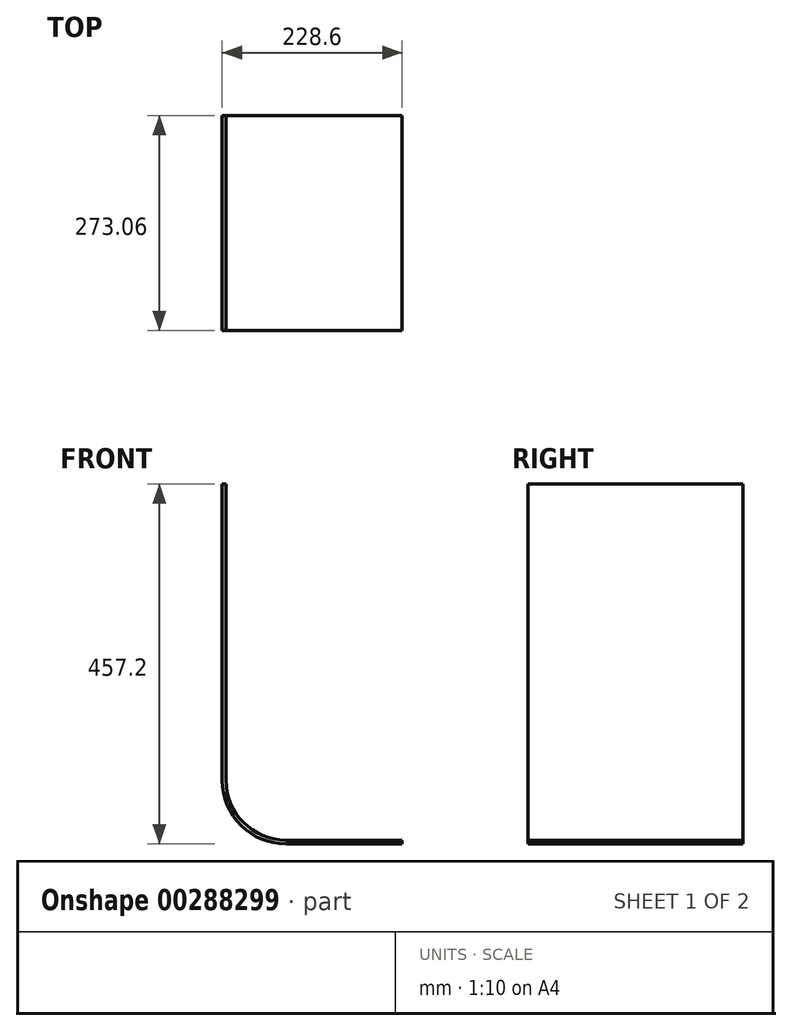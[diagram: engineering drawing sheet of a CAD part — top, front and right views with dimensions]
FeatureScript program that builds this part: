
annotation { "Feature Type Name" : "Feature", "Feature Type Description" : "" }
export const myFeature = defineFeature(function(context is Context, id is Id, definition is map)
    precondition{}
    {
        {
            var Q0;
            Q0=qCreatedBy(makeId("Front.planeOp"),FACE);
            var sketch = newSketch(context, id + "F0", { "sketchPlane" : qUnion([Q0])});
            skLineSegment(sketch, "E0", {"start": v(0, 161.93) * mm, "end": v(0, 914.4) * mm});
            skLineSegment(sketch, "E1", {"start": v(161.93, 0) * mm, "end": v(457.2, 0) * mm});
            skArc(sketch, "E2", {"start": v(0, 161.92) * mm, "mid": v(47.43, 47.43) * mm, "end": v(161.93, 0) * mm});
            skLineSegment(sketch, "E3.0", {"start": v(9.53, 161.93) * mm, "end": v(9.53, 914.4) * mm});
            skArc(sketch, "E3.1", {"start": v(9.53, 161.93) * mm, "mid": v(54.16, 54.16) * mm, "end": v(161.92, 9.53) * mm});
            skLineSegment(sketch, "E3.2", {"start": v(161.92, 9.53) * mm, "end": v(457.2, 9.53) * mm});
            skLineSegment(sketch, "E4", {"start": v(9.53, 914.4) * mm, "end": v(0, 914.4) * mm});
            skLineSegment(sketch, "E5", {"start": v(457.2, 9.53) * mm, "end": v(457.2, 0) * mm});
            skSolve(sketch);
        }
        {
            var Q0;
            Q0=qSketchRegion(id+"F0",true);
            extrude(context, id + "F1", {"entities" : qUnion([Q0]), "endBound" : BoundingType.SYMMETRIC, "depth" : 546.1 * mm});
        }
        {
            var Q0;
            Q0=makeQuery(id+"F1.opExtrude","SWEPT_BODY",BODY,{"disambiguationData":[OSD([sQuery(id+"F0.wireOp",EDGE,"E0"),sQuery(id+"F0.wireOp",EDGE,"E1"),sQuery(id+"F0.wireOp",EDGE,"E2"),sQuery(id+"F0.wireOp",EDGE,"E3.0"),sQuery(id+"F0.wireOp",EDGE,"E3.1"),sQuery(id+"F0.wireOp",EDGE,"E3.2"),sQuery(id+"F0.wireOp",EDGE,"E4"),sQuery(id+"F0.wireOp",EDGE,"E5")])]});
            var Q1;
            Q1=qCreatedBy(makeId("Origin.pointOp"),VERTEX);
            transform(context, id + "F2", {"entities" : qUnion([Q0]), "transformType" : TransformType.SCALE_UNIFORMLY, "scale" : 0.5, "scalePoint" : qUnion([Q1]), "makeCopy" : false});
        }
    });
